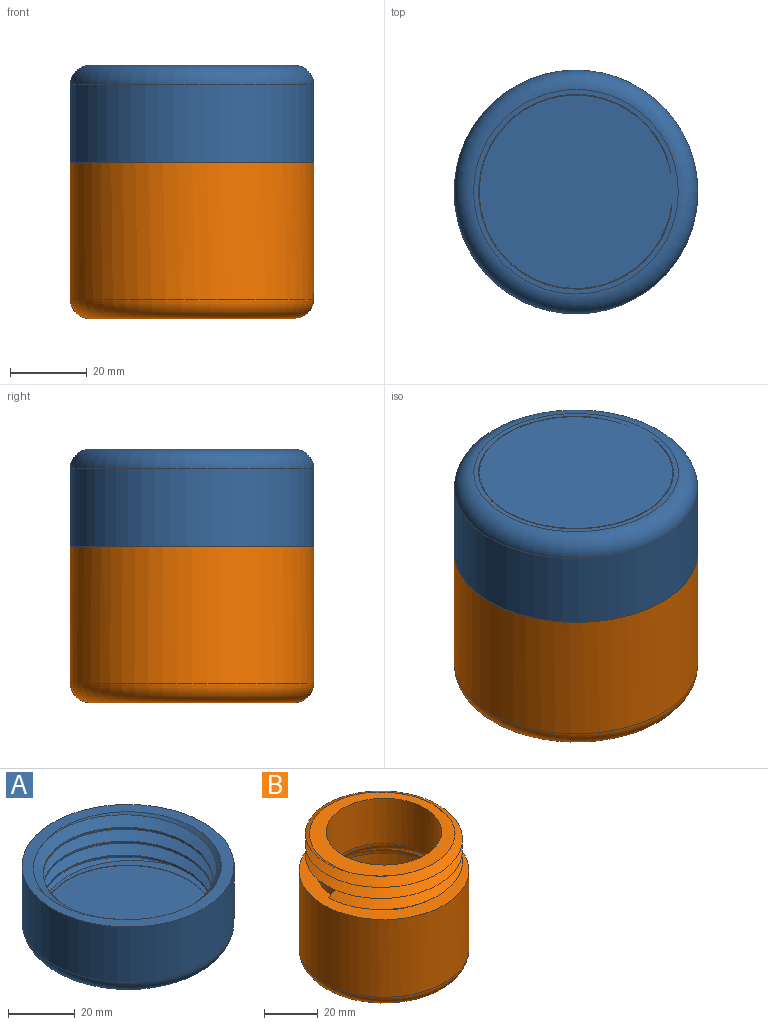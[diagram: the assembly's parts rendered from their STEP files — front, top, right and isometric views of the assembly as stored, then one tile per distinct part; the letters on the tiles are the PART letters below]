
ASSEMBLY  parts=2 mates=1
PART A: 14 faces, bbox 71.3x71.3x32.8 mm
  f0: bspline ~67.34x58.32mm, area 54.9mm2, adj f3,f5,f7,f12
  f1: bspline ~67.34x58.32mm, area 54.9mm2, adj f3,f5,f7,f12
  f2: cylinder r=25.4mm len=50.8mm, axis (0,0,-1), area 353mm2, adj f5,f6,f8,f9
  f3: plane 53.38x53.38mm, normal (0,0,-1), area 2206.8mm2, adj f0,f1,f7,f12,f13
  f4: plane 64.09x64.09mm, normal (0,0,1), area 684.3mm2, adj f6,f8,f9,f10
  f5: plane 50.64x50.44mm, normal (0,0,1), area 1999mm2, adj f0,f1,f2,f7
  f6: cone r=25.4mm half-angle=45deg, axis (0,0,1), area 264.1mm2, adj f2,f4,f8,f9
  f7: cylinder r=25.2mm len=50.4mm, axis (0,0,1), area 1086.1mm2, adj f0,f1,f3,f5
  f8: bspline ~67.34x58.32mm, area 2484.1mm2, adj f2,f4,f6,f9,f11
  f9: bspline ~67.34x58.32mm, area 2484.3mm2, adj f2,f4,f6,f8,f11
  f10: cylinder r=31.75mm len=63.5mm, axis (0,0,-1), area 4053.7mm2, adj f4,f13
  f11: plane 56.62x55.97mm, normal (0,0,1), area 269.2mm2, adj f8,f9,f12
  f12: cylinder r=25.4mm len=50.8mm, axis (0,0,-1), area 1039.3mm2, adj f0,f1,f3,f11
  f13: torus R=26.67mm, axis (0,0,1), area 1499.3mm2, adj f3,f10
PART B: 15 faces, bbox 71.6x71.6x64.2 mm
  f0: bspline ~67.8x58.72mm, area 2573.7mm2, adj f1,f3,f4,f6
  f1: bspline ~67.8x58.72mm, area 2225.9mm2, adj f0,f3,f4,f6
  f2: plane 63.5x63.5mm, normal (0,0,1), area 1140.1mm2, adj f3,f7
  f3: cylinder r=25.4mm len=50.8mm, axis (0,0,-1), area 605.7mm2, adj f0,f1,f2,f4,f6
  f4: plane 57.32x57.3mm, normal (0,0,1), area 861.4mm2, adj f0,f1,f3,f5
  f5: cylinder r=21.59mm len=43.18mm, axis (0,0,1), area 2800.3mm2, adj f4,f12
  f6: plane 4.57x3.96mm, normal (0,1,0), area 9.1mm2, adj f0,f1,f3
  f7: cylinder r=31.75mm len=63.5mm, axis (0,0,-1), area 7093.9mm2, adj f2,f14
  f8: cylinder r=29.21mm len=58.42mm, axis (0,0,1), area 2797mm2, adj f9,f13
  f9: torus R=24.13mm, axis (0,0,1), area 1172.2mm2, adj f8,f12
  f10: plane 48.26x48.26mm, normal (0,0,1), area 1829.2mm2, adj f13
  f11: plane 53.34x53.34mm, normal (0,0,-1), area 2234.6mm2, adj f14
  f12: torus R=26.67mm, axis (0,0,-1), area 965.1mm2, adj f5,f9
  f13: torus R=24.13mm, axis (0,0,-1), area 1372mm2, adj f8,f10
  f14: torus R=26.67mm, axis (0,0,-1), area 1499.3mm2, adj f7,f11
PLACE A rot(axis=(-1,0,0),180deg) t=(60.03,91.4,104.85)mm
PLACE B t=(60.03,91.4,71.83)mm
MATE cylindrical B.f5 <-> A.f2  axis (0,0,1) through (60.03,91.4,97.23)mm
